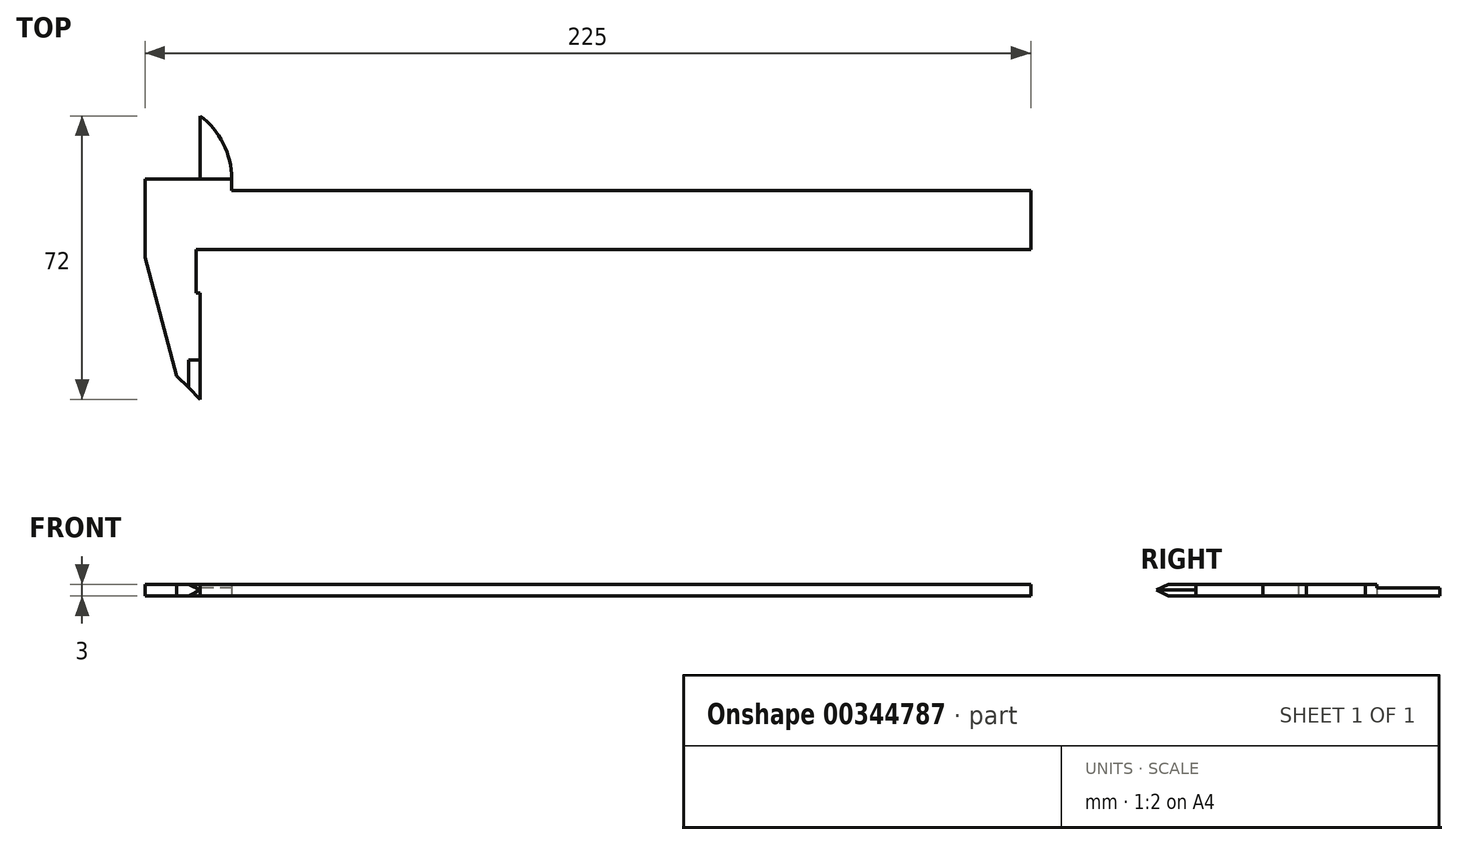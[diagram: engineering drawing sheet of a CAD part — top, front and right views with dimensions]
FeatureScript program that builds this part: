
annotation { "Feature Type Name" : "Feature", "Feature Type Description" : "" }
export const myFeature = defineFeature(function(context is Context, id is Id, definition is map)
    precondition{}
    {
        {
            var Q0;
            Q0=qCreatedBy(makeId("Top.planeOp"),FACE);
            var sketch = newSketch(context, id + "F0", { "sketchPlane" : qUnion([Q0])});
            skLineSegment(sketch, "E0.bottom", {"start": v(0, 0) * mm, "end": v(-203, 0) * mm});
            skLineSegment(sketch, "E0.top", {"start": v(0, -15) * mm, "end": v(-212, -15) * mm});
            skLineSegment(sketch, "E0.left", {"start": v(0, 0) * mm, "end": v(0, -15) * mm});
            skLineSegment(sketch, "E1", {"start": v(-225, -17) * mm, "end": v(-216.95, -47.05) * mm});
            skLineSegment(sketch, "E2", {"start": v(-216.95, -47.05) * mm, "end": v(-211, -53) * mm});
            skLineSegment(sketch, "E3", {"start": v(-211, -53) * mm, "end": v(-211, -26) * mm});
            skLineSegment(sketch, "E4", {"start": v(-211, -26) * mm, "end": v(-212, -26) * mm});
            skLineSegment(sketch, "E5", {"start": v(-212, -26) * mm, "end": v(-212, -15) * mm});
            skLineSegment(sketch, "E6", {"start": v(-225, -17) * mm, "end": v(-225, 3) * mm});
            skLineSegment(sketch, "E7", {"start": v(-225, 3) * mm, "end": v(-203, 3) * mm});
            skLineSegment(sketch, "E8", {"start": v(-203, 3) * mm, "end": v(-203, 0) * mm});
            skLineSegment(sketch, "E9", {"start": v(-211, 3) * mm, "end": v(-211, 19) * mm});
            skArc(sketch, "E10", {"start": v(-203, 3) * mm, "mid": v(-205.11, 11.94) * mm, "end": v(-211, 19) * mm});
            skSolve(sketch);
        }
        {
            var Q0;
            Q0=makeQuery(id+"F0.imprint","IMPRINT",FACE,{"disambiguationData":[TD([[makeQuery(id+"F0.imprint","IMPRINT",EDGE,{"derivedFrom":sQuery(id+"F0.wireOp",EDGE,"E0.bottom")}),1.0]])]});
            var Q1;
            {var subQ2=sQuery(id+"F0.wireOp",EDGE,"E9");Q1=makeQuery(id+"F0.imprint","IMPRINT",FACE,{"disambiguationData":[TD([[makeQuery(id+"F0.imprint","IMPRINT",EDGE,{"derivedFrom":subQ2}),-1.0]])]});}
            extrude(context, id + "F1", {"entities" : qUnion([Q0, Q1]), "depth" : 3 * mm});
        }
        {
            var Q0;
            Q0=makeQuery(id+"F1.opExtrude","SWEPT_FACE",FACE,{"disambiguationData":[OSD([sQuery(id+"F0.wireOp",EDGE,"E9")])]});
            var sketch = newSketch(context, id + "F2", { "sketchPlane" : qUnion([Q0])});
            skLineSegment(sketch, "E11.bottom", {"start": v(-3, 3) * mm, "end": v(-19, 3) * mm});
            skLineSegment(sketch, "E11.top", {"start": v(-3, 2) * mm, "end": v(-19, 2) * mm});
            skLineSegment(sketch, "E11.left", {"start": v(-3, 3) * mm, "end": v(-3, 2) * mm});
            skLineSegment(sketch, "E11.right", {"start": v(-19, 3) * mm, "end": v(-19, 2) * mm});
            skSolve(sketch);
        }
        {
            var Q0;
            Q0=makeQuery(id+"F2.imprint","IMPRINT",FACE,{"disambiguationData":[TD([[makeQuery(id+"F2.imprint","IMPRINT",EDGE,{"derivedFrom":sQuery(id+"F2.wireOp",EDGE,"E11.bottom")}),1.0]])]});
            extrude(context, id + "F3", {"entities" : qUnion([Q0]), "operationType" : NewBodyOperationType.REMOVE, "oppositeDirection" : true, "depth" : 10 * mm});
        }
        {
            var Q0;
            Q0=qCreatedBy(makeId("Front.planeOp"),FACE);
            cPlane(context, id + "F4", {"entities" : qUnion([Q0]), "cplaneType" : CPlaneType.OFFSET, "offset" : 53 * mm, "width" : 150 * mm, "height" : 150 * mm});
        }
        {
            var Q0;
            Q0=qCreatedBy(id+"F4.planeOp",FACE);
            var sketch = newSketch(context, id + "F5", { "sketchPlane" : qUnion([Q0])});
            skLineSegment(sketch, "E12", {"start": v(-211, 1.5) * mm, "end": v(-214, 3) * mm});
            skLineSegment(sketch, "E13", {"start": v(-214, 3) * mm, "end": v(-206, 3) * mm});
            skLineSegment(sketch, "E14", {"start": v(-206, 3) * mm, "end": v(-206, 0) * mm});
            skLineSegment(sketch, "E15", {"start": v(-206, 0) * mm, "end": v(-214, 0) * mm});
            skLineSegment(sketch, "E16", {"start": v(-214, 0) * mm, "end": v(-211, 1.5) * mm});
            skSolve(sketch);
        }
        {
            var Q0;
            Q0=makeQuery(id+"F5.imprint","IMPRINT",FACE,{"disambiguationData":[TD([[makeQuery(id+"F5.imprint","IMPRINT",EDGE,{"derivedFrom":sQuery(id+"F5.wireOp",EDGE,"E12")}),-1.0]])]});
            extrude(context, id + "F6", {"entities" : qUnion([Q0]), "operationType" : NewBodyOperationType.REMOVE, "oppositeDirection" : true, "depth" : 10 * mm});
        }
    });
